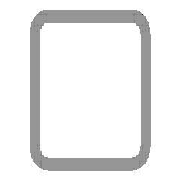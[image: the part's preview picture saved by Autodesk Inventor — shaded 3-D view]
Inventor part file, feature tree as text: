
AUTODESK INVENTOR PART (.ipt)
format: ipt  version: 2025.1 (Build 291241020, 241B)  size: 142,336 bytes
history: native  units: mm (DEFAULTED — no unit token found)
features: other x4, sketch x1, plane x1
ambient origin geometry x8: Origin, YZ Plane, XZ Plane, XY Plane, X Axis, Y Axis, Z Axis, Center Point
bodies: Solid1 (feature_tree), Body (feature_tree)
feature tree (6):
  parser-record x1  (decoder bookkeeping rows leaked as tree rows — omitted from the tree; the rows remain in map.json)
  other  "Driven Length"
  other  "Start Plane"
  other  "End Plane"
  sketch  "Sketch3"  dims[d3=950.0mm d4=0.0mm d7=4.0mm d9=40.0mm d11=40.0mm d12=2.0mm d13=50.0mm d14=1000.0mm d15=20.0mm d16=20.0mm d17=90.0deg d18=950.0mm]
  plane  "Work Plane3"
